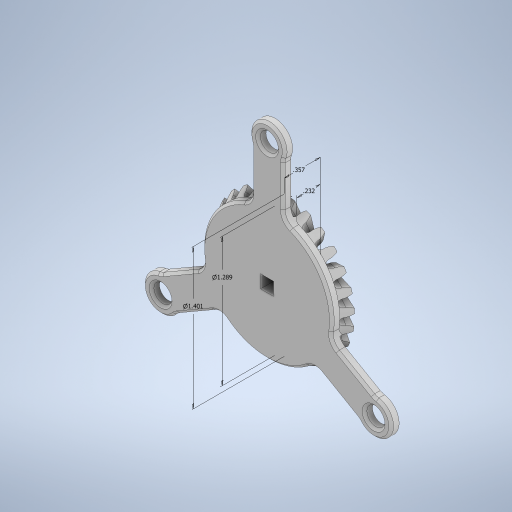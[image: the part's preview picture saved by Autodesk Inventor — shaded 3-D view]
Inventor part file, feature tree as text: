
AUTODESK INVENTOR PART (.ipt)
format: ipt  version: 2023 (Build 270158000, 158)  size: 3,036,672 bytes
history: native  units: in
note: dims shown in document units (in); Inventor stores cm internally (conversion verified against a paired STEP export)
features: sketch x4, extrude x3, move_body x2, other x2, pattern_circular x2, revolve x1, loft x1, boolean_combine x1, fillet x1, chamfer x1
ambient origin geometry x8: Origin, YZ Plane, XZ Plane, XY Plane, X Axis, Y Axis, Z Axis, Center Point
bodies: Solid3 (feature_tree), Solid4 (feature_tree), Solid5 (feature_tree)
feature tree (18):
  sketch  "Sketch1"  dims[d3=1.289in d4=1.401in]
  revolve  "Revolution1"  [1 undecoded]
  extrude  "Extrusion2"  Depth=0.232in
  move_body  "Move Body1"
  move_body  "Move Body2"
  other  "Work Point1"
  loft  "Loft1"
  boolean_combine  "Combine1"
  pattern_circular  "Circular Pattern1"  [2 undecoded]
  extrude  "Extrusion3"  TaperAngle=0.0deg  [1 undecoded]
  fillet  "Fillet1"  [1 undecoded]
  pattern_circular  "Circular Pattern2"  Count=27 Angle=360.0deg
  extrude  "Extrusion4"  Depth=0.18in
  chamfer  "Chamfer2"  Distance=0.3125in
  sketch  "Sketch2"  dims[d5=0.357in d6=0.232in]
  other  "Edges1"
  sketch  "Sketch3"  dims[d7=90.0deg d8=0.0039in d9=0.0in]
  sketch  "Sketch4"  dims[d10=0.4078in d11=0.0in d12=-0.019in d13=-0.102in d14=0.0in d15=90.0deg d16=0.0in d17=90.0deg d18=10.6299in d19=360.0deg d21=0.18in d23=0.3125in d25=2.45in d26=0.35in d27=1.1811in d29=360.0deg d31=0.0787in d32=0.0in d33=0.125in d34=1.1811in d35=360.0deg d40=0.13in d41=0.13in d42=0.0in d43=0.0in d44=0.0236in d45=0.125in d46=45.0deg]
note: 5 required parameter values undecoded (feature->parameter linkage not recoverable at this tier; creation-order binding heuristic only, values carry confidence <= 0.55)